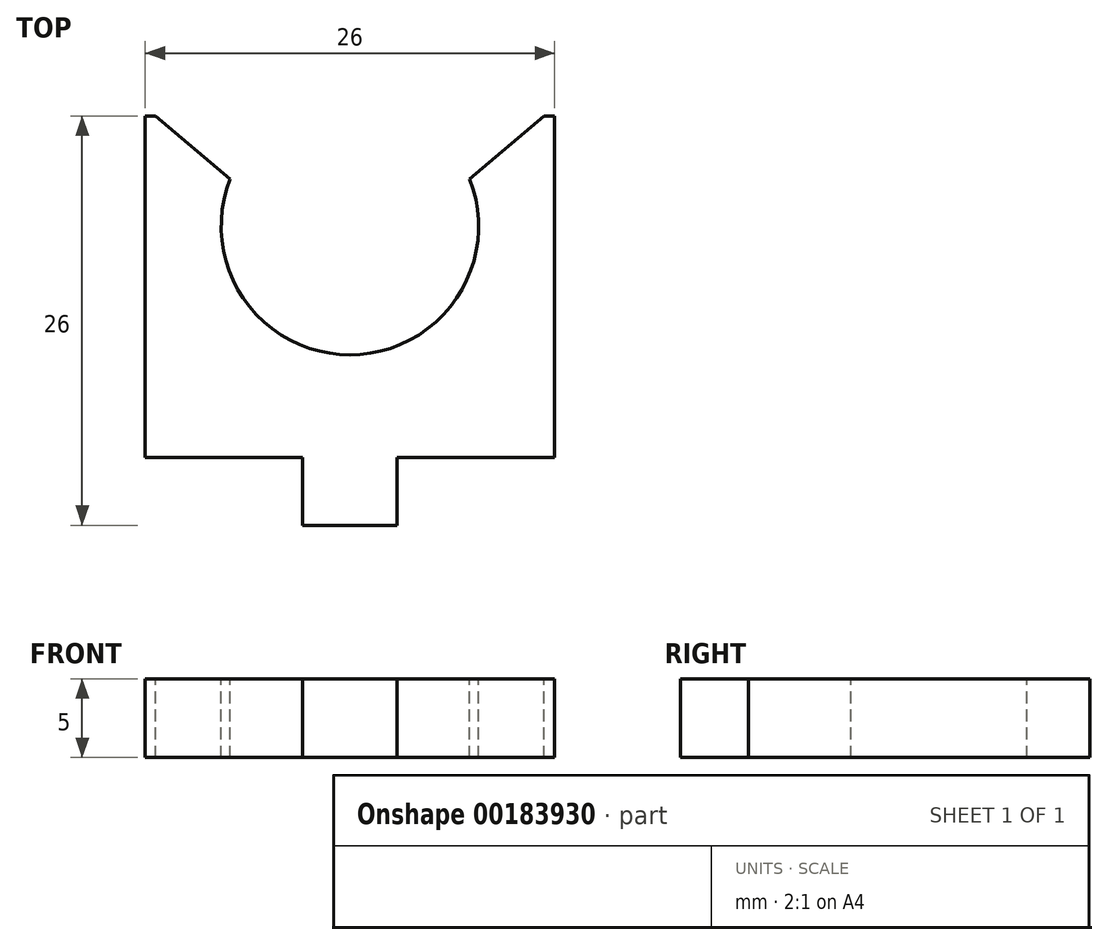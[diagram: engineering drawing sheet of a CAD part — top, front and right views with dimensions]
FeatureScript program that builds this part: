
annotation { "Feature Type Name" : "Feature", "Feature Type Description" : "" }
export const myFeature = defineFeature(function(context is Context, id is Id, definition is map)
    precondition{}
    {
        {
            var Q0;
            Q0=qCreatedBy(makeId("Top.planeOp"),FACE);
            var sketch = newSketch(context, id + "F0", { "sketchPlane" : qUnion([Q0])});
            skLineSegment(sketch, "E0.bottom", {"start": v(13, -13) * mm, "end": v(-13, -13) * mm});
            skLineSegment(sketch, "E0.top", {"start": v(13, 13) * mm, "end": v(-13, 13) * mm});
            skLineSegment(sketch, "E0.left", {"start": v(13, -13) * mm, "end": v(13, 13) * mm});
            skLineSegment(sketch, "E0.right", {"start": v(-13, -13) * mm, "end": v(-13, 13) * mm});
            skPoint(sketch, "E0.middle", {"position": v(0, 0) * mm});
            skSolve(sketch);
        }
        {
            var Q0;
            Q0 = qSketchRegion(id + "F0", true);
            extrude(context, id + "F1", {"entities" : qUnion([Q0]), "depth" : 5 * mm});
        }
        {
            var Q0;
            Q0=makeQuery(id+"F1.opExtrude","CAP_FACE",FACE,{"disambiguationData":[OSD([sQuery(id+"F0.wireOp",EDGE,"E0.bottom"),sQuery(id+"F0.wireOp",EDGE,"E0.top"),sQuery(id+"F0.wireOp",EDGE,"E0.left"),sQuery(id+"F0.wireOp",EDGE,"E0.right")])],"isStart":false});
            var sketch = newSketch(context, id + "F2", { "sketchPlane" : qUnion([Q0])});
            skCircle(sketch, "E1", {"center": v(0, 6) * mm, "radius": 8.18 * mm});
            skLineSegment(sketch, "E2", {"start": v(-7.6, 9) * mm, "end": v(-12.33, 13) * mm});
            skLineSegment(sketch, "E3", {"start": v(-12.33, 13) * mm, "end": v(12.33, 13) * mm});
            skLineSegment(sketch, "E4", {"start": v(7.6, 9) * mm, "end": v(12.33, 13) * mm});
            skSolve(sketch);
        }
        {
            var Q0;
            Q0 = qSketchRegion(id + "F2", true);
            extrude(context, id + "F3", {"entities" : qUnion([Q0]), "operationType" : NewBodyOperationType.REMOVE, "oppositeDirection" : true, "depth" : 25 * mm});
        }
        {
            var Q0;
            Q0=makeQuery(id+"F1.opExtrude","CAP_FACE",FACE,{"disambiguationData":[OSD([sQuery(id+"F0.wireOp",EDGE,"E0.bottom"),sQuery(id+"F0.wireOp",EDGE,"E0.top"),sQuery(id+"F0.wireOp",EDGE,"E0.left"),sQuery(id+"F0.wireOp",EDGE,"E0.right")])],"isStart":false});
            var sketch = newSketch(context, id + "F4", { "sketchPlane" : qUnion([Q0])});
            skLineSegment(sketch, "E5.bottom", {"start": v(-13, -13) * mm, "end": v(-3, -13) * mm});
            skLineSegment(sketch, "E5.top", {"start": v(-13, -8.7) * mm, "end": v(-3, -8.7) * mm});
            skLineSegment(sketch, "E5.left", {"start": v(-13, -13) * mm, "end": v(-13, -8.7) * mm});
            skLineSegment(sketch, "E5.right", {"start": v(-3, -13) * mm, "end": v(-3, -8.7) * mm});
            skPoint(sketch, "E6.oppositeSnap0", {"position": v(0, -13) * mm});
            skLineSegment(sketch, "E6.bottom", {"start": v(0, 0) * mm, "end": v(0, 0) * mm});
            skLineSegment(sketch, "E6.top", {"start": v(0, -18.05) * mm, "end": v(0, -18.05) * mm});
            skLineSegment(sketch, "E6.left", {"start": v(0, 0) * mm, "end": v(0, -18.05) * mm, "construction": true});
            skLineSegment(sketch, "E6.right", {"start": v(0, 0) * mm, "end": v(0, -18.05) * mm, "construction": true});
            skLineSegment(sketch, "E7.MirrorCS", {"start": v(13, -8.7) * mm, "end": v(3, -8.7) * mm});
            skLineSegment(sketch, "E8.MirrorCS", {"start": v(3, -13) * mm, "end": v(3, -8.7) * mm});
            skLineSegment(sketch, "E9.MirrorCS", {"start": v(13, -13) * mm, "end": v(3, -13) * mm});
            skLineSegment(sketch, "E10.MirrorCS", {"start": v(13, -13) * mm, "end": v(13, -8.7) * mm});
            skSolve(sketch);
        }
        {
            var Q0;
            Q0 = qSketchRegion(id + "F4", true);
            extrude(context, id + "F5", {"entities" : qUnion([Q0]), "operationType" : NewBodyOperationType.REMOVE, "oppositeDirection" : true, "depth" : 25 * mm});
        }
    });
